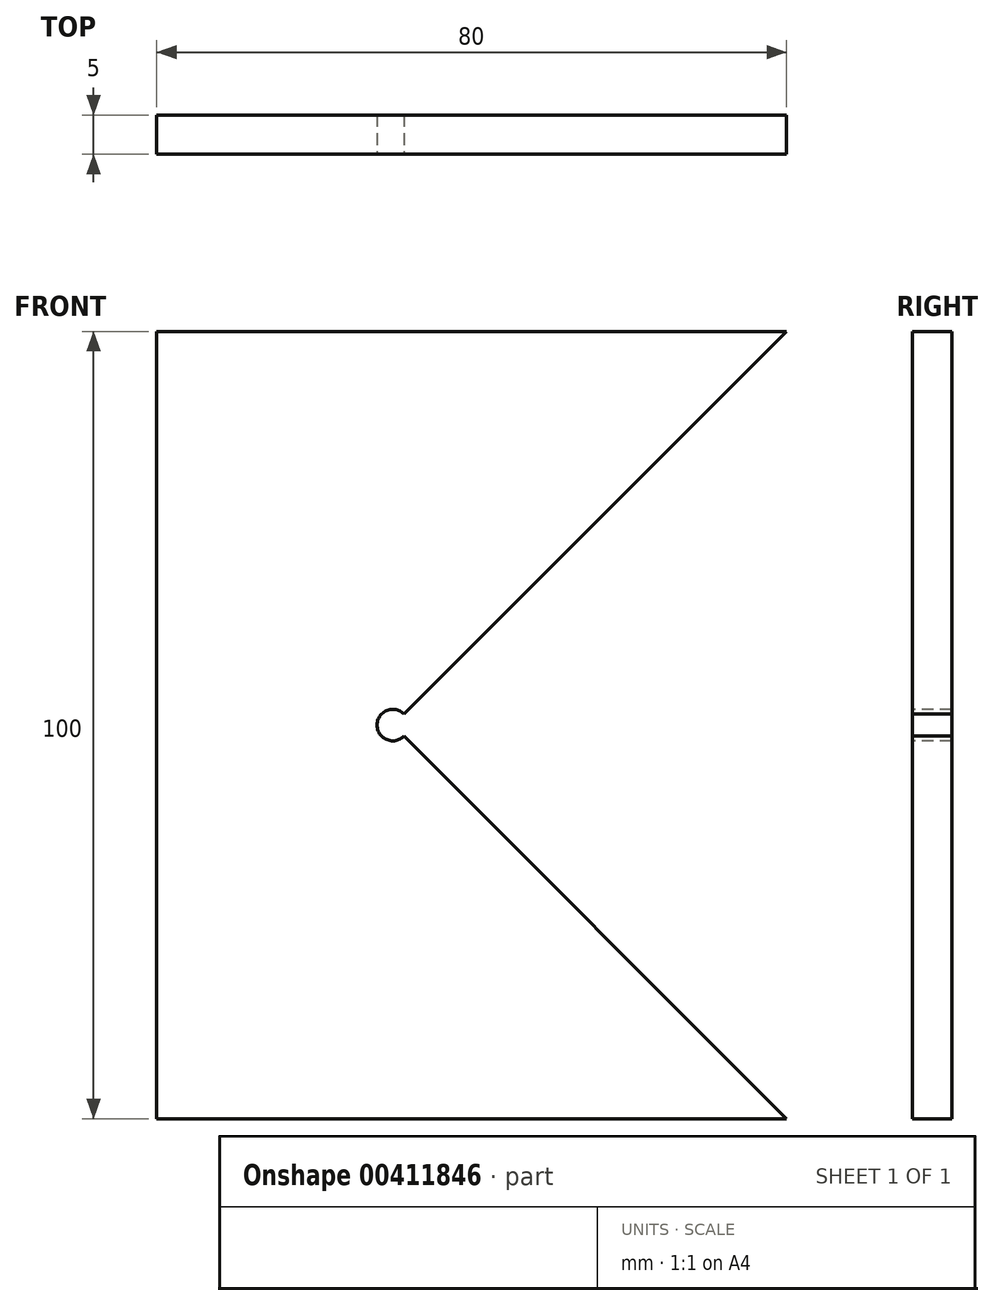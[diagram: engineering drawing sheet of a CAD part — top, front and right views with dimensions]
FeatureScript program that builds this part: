
annotation { "Feature Type Name" : "Feature", "Feature Type Description" : "" }
export const myFeature = defineFeature(function(context is Context, id is Id, definition is map)
    precondition{}
    {
        {
            var Q0;
            Q0=qCreatedBy(makeId("Front.planeOp"),FACE);
            var sketch = newSketch(context, id + "F0", { "sketchPlane" : qUnion([Q0])});
            skLineSegment(sketch, "E0", {"start": v(0, 0) * mm, "end": v(0, 100) * mm});
            skLineSegment(sketch, "E1", {"start": v(0, 100) * mm, "end": v(80, 100) * mm});
            skLineSegment(sketch, "E2", {"start": v(80, 100) * mm, "end": v(30, 50) * mm});
            skLineSegment(sketch, "E3", {"start": v(30, 50) * mm, "end": v(80, 0) * mm});
            skLineSegment(sketch, "E4", {"start": v(80, 0) * mm, "end": v(0, 0) * mm});
            skLineSegment(sketch, "E5", {"start": v(80, 100) * mm, "end": v(80, 0) * mm, "construction": true});
            skLineSegment(sketch, "E6", {"start": v(30, 50) * mm, "end": v(0, 50) * mm, "construction": true});
            skSolve(sketch);
        }
        {
            var Q0;
            Q0 = qSketchRegion(id + "F0", true);
            extrude(context, id + "F1", {"entities" : qUnion([Q0]), "depth" : 5 * mm});
        }
        {
            var Q0;
            Q0=makeQuery(id+"F1.opExtrude","CAP_FACE",FACE,{"disambiguationData":[OSD([sQuery(id+"F0.wireOp",EDGE,"E0"),sQuery(id+"F0.wireOp",EDGE,"E1"),sQuery(id+"F0.wireOp",EDGE,"E2"),sQuery(id+"F0.wireOp",EDGE,"E3"),sQuery(id+"F0.wireOp",EDGE,"E4")])],"isStart":false});
            var sketch = newSketch(context, id + "F2", { "sketchPlane" : qUnion([Q0])});
            skCircle(sketch, "E7", {"center": v(30, 50) * mm, "radius": 2 * mm});
            skSolve(sketch);
        }
        {
            var Q0;
            Q0 = qSketchRegion(id + "F2", true);
            extrude(context, id + "F3", {"entities" : qUnion([Q0]), "operationType" : NewBodyOperationType.REMOVE, "endBound" : BoundingType.THROUGH_ALL, "oppositeDirection" : true, "depth" : 25 * mm});
        }
    });
